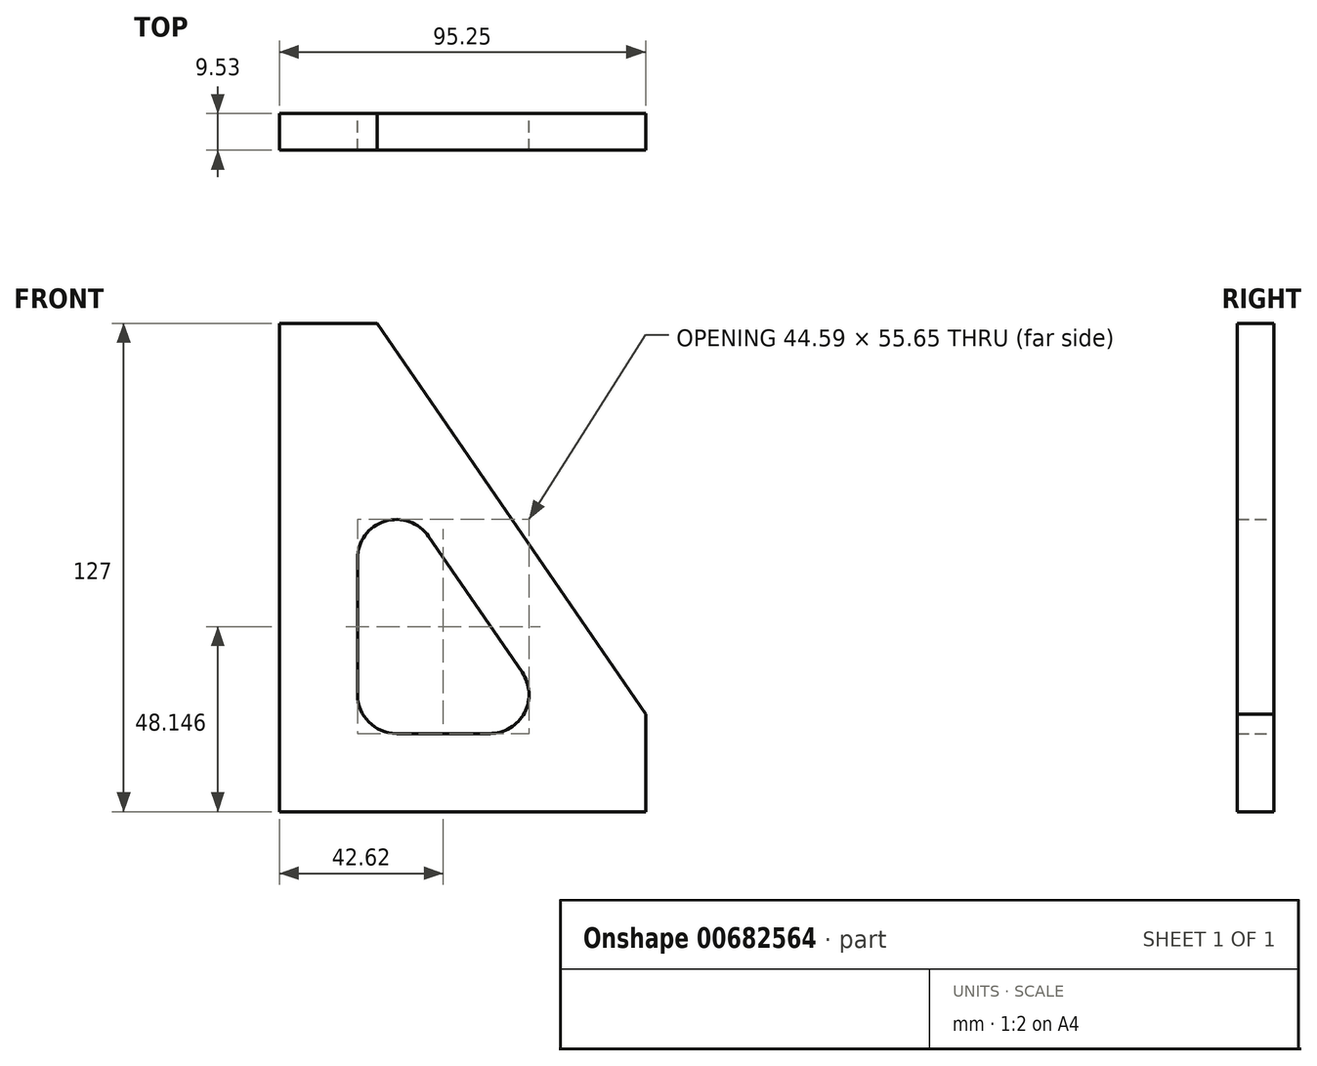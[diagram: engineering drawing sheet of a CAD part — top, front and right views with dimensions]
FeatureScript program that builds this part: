
annotation { "Feature Type Name" : "Feature", "Feature Type Description" : "" }
export const myFeature = defineFeature(function(context is Context, id is Id, definition is map)
    precondition{}
    {
        {
            var Q0;
            Q0=qCreatedBy(makeId("Front.planeOp"),FACE);
            var sketch = newSketch(context, id + "F0", { "sketchPlane" : qUnion([Q0])});
            skLineSegment(sketch, "E0", {"start": v(-81.5, 72.88) * mm, "end": v(-81.5, -54.12) * mm});
            skLineSegment(sketch, "E1", {"start": v(-81.5, 72.88) * mm, "end": v(-56.1, 72.88) * mm});
            skLineSegment(sketch, "E2", {"start": v(13.75, -28.72) * mm, "end": v(13.75, -54.12) * mm});
            skLineSegment(sketch, "E3", {"start": v(13.75, -54.12) * mm, "end": v(-81.5, -54.12) * mm});
            skLineSegment(sketch, "E4", {"start": v(-56.1, 72.88) * mm, "end": v(13.75, -28.72) * mm});
            skLineSegment(sketch, "E5.0", {"start": v(-42.64, 17.45) * mm, "end": v(-18.35, -17.88) * mm});
            skLineSegment(sketch, "E6.0", {"start": v(-61.18, 11.7) * mm, "end": v(-61.18, -23.64) * mm});
            skLineSegment(sketch, "E7.0", {"start": v(-26.73, -33.8) * mm, "end": v(-51.02, -33.8) * mm});
            skArc(sketch, "E8.filletArc", {"start": v(-42.64, 17.45) * mm, "mid": v(-54.03, 21.4) * mm, "end": v(-61.18, 11.7) * mm});
            skArc(sketch, "E9.filletArc", {"start": v(-61.18, -23.64) * mm, "mid": v(-58.2, -30.82) * mm, "end": v(-51.02, -33.8) * mm});
            skArc(sketch, "E10.filletArc", {"start": v(-26.73, -33.8) * mm, "mid": v(-17.73, -28.37) * mm, "end": v(-18.35, -17.88) * mm});
            skSolve(sketch);
        }
        {
            var Q0;
            Q0 = qSketchRegion(id + "F0", true);
            extrude(context, id + "F1", {"entities" : qUnion([Q0]), "depth" : 9.52 * mm, "offsetDistance" : 25.4 * mm});
        }
    });
